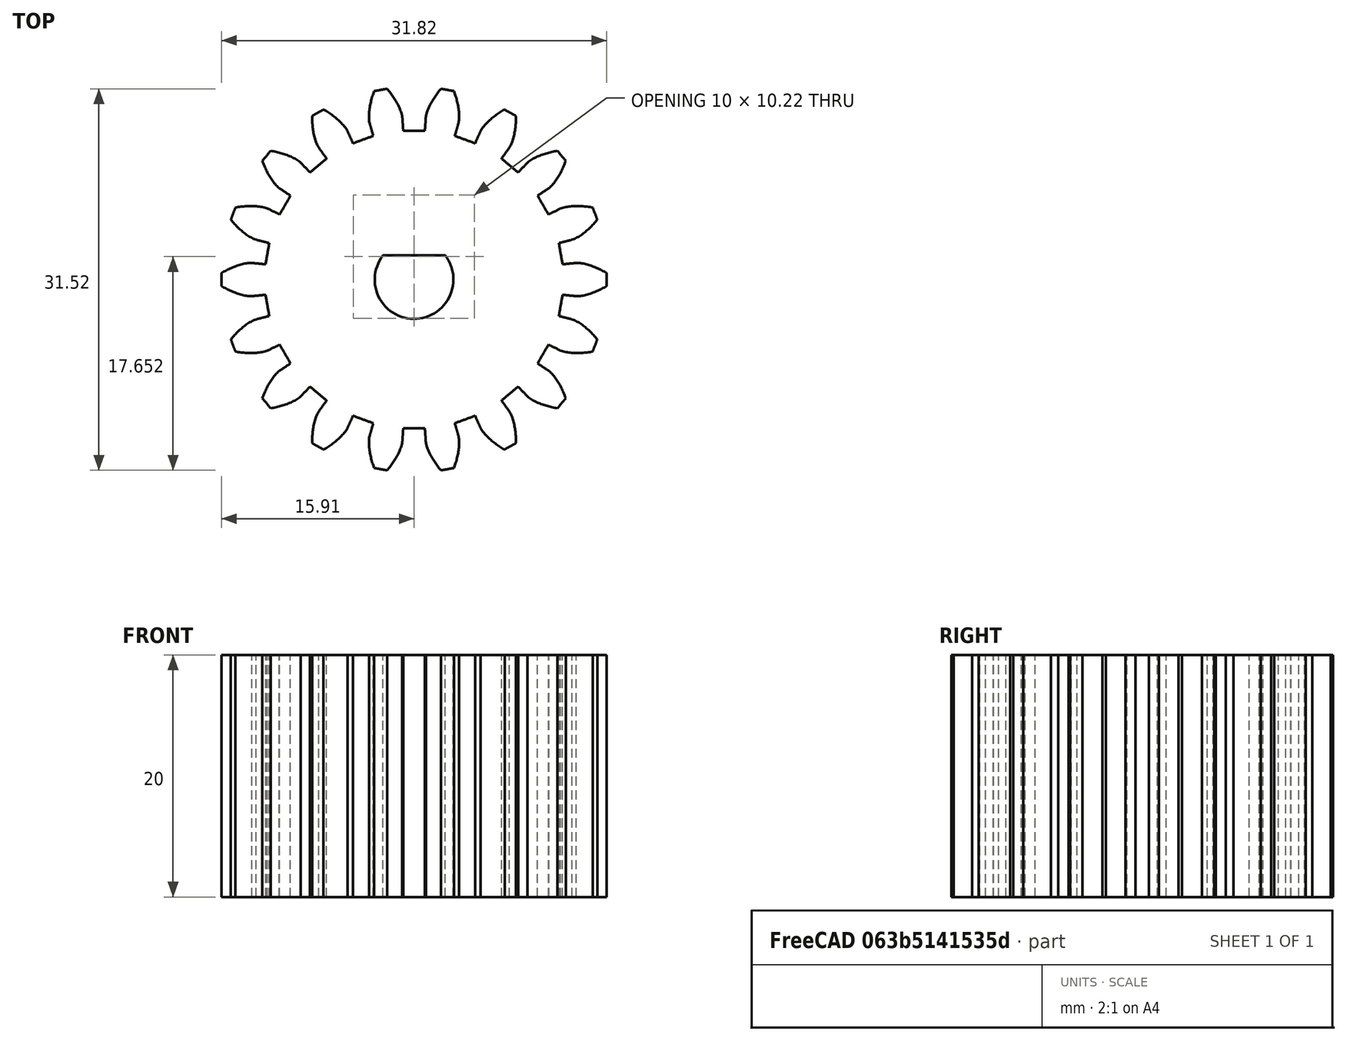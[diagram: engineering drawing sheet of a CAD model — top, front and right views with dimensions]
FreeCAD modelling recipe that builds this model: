
FCSTD DOCUMENT  (FreeCAD 0.18R16110 (Git))
Label: Cogwheel
License: All rights reserved
LicenseURL: http://en.wikipedia.org/wiki/All_rights_reserved
objects: Part::FeaturePython×1, Part::Cylinder×1, Part::Box×1, Part::Cut×1, Part::MultiFuse×1
note: 5 computed .brp shape members not serialized (recipe doc carries the construction recipe); baked Part::Feature solids carry a one-line shape summary decoded from their .brp

FEATURE [Part::FeaturePython] InvoluteGear  # WARN: FeaturePython — macro-defined, semantics opaque (R4)
  backlash = 0
  beta = 0
  clearance = 0.25
  double_helix = false
  head = 0
  height = 20
  module = 1.59155
  numpoints = 6
  pressure_angle = 20
  reversed_backlash = false
  shift = 0
  simple = false
  teeth = 18
  undercut = false
  expr: module = 5 / pi
FEATURE [Part::Cylinder] Cylinder
  Angle = 360
  AttacherType = Attacher::AttachEngine3D
  Height = 20
  Radius = 3.25
FEATURE [Part::Box] Box  label="Cube"
  AttacherType = Attacher::AttachEngine3D
  Height = 20
  Length = 10
  Placement = pos=(-5,2,0) rot=(0,0,1;0rad)
  Width = 5
FEATURE [Part::Cut] Cut
  Base = -> InvoluteGear
  Tool = -> Cylinder
FEATURE [Part::MultiFuse] Fusion
  Shapes = -> [Box,Cut]
